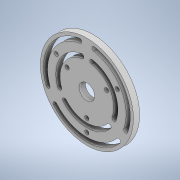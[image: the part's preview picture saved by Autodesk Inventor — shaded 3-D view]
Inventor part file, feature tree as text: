
AUTODESK INVENTOR PART (.ipt)
format: ipt  version: 2021 (Build 250183000, 183)  size: 193,024 bytes
history: native  units: mm
features: extrude x2, sketch x2, pattern_circular x1
ambient origin geometry x8: Origin, YZ Plane, XZ Plane, XY Plane, X Axis, Y Axis, Z Axis, Center Point
bodies: Solid1 (feature_tree)
feature tree (5):
  extrude  "Extrusion1"  Depth=6.0mm TaperAngle=0.0deg
  extrude  "Extrusion2"  TaperAngle=0.0deg  [1 undecoded]
  pattern_circular  "Circular Pattern2"  [2 undecoded]
  sketch  "Sketch1"  dims[d0=90.0mm d1=6.0mm d2=0.0mm]
  sketch  "Sketch2"  dims[d3=15.0mm d12=0.0mm d13=0.0mm d35=17.453293mm d36=4.0mm d37=28.0mm d38=17.453293mm d39=4.0mm d40=12.0mm d41=4.0mm d42=4.0mm d43=22.0mm d44=34.0mm d45=30.0mm d46=360.0deg]
note: 3 required parameter values undecoded (feature->parameter linkage not recoverable at this tier; creation-order binding heuristic only, values carry confidence <= 0.55)
